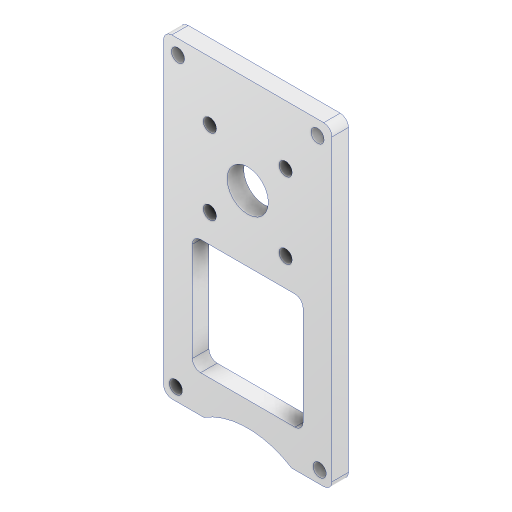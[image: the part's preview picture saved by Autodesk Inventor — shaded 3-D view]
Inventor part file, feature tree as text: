
AUTODESK INVENTOR PART (.ipt)
format: ipt  version: 2023.2 (Build 272271000, 271)  size: 305,664 bytes
history: native  units: mm
features: sketch x6, extrude x6, projected_geometry x4, fillet x1
ambient origin geometry x8: Origin, YZ Plane, XZ Plane, XY Plane, X Axis, Y Axis, Z Axis, Center Point
bodies: Body1 (feature_tree)
feature tree (17):
  sketch  "스케치1"
  extrude  "돌출2"  Depth=68.5mm
  sketch  "스케치4"
  extrude  "돌출4"  Depth=4.0mm TaperAngle=0.0deg
  extrude  "돌출3"  Depth=3.2mm
  extrude  "돌출6"  Depth=3.2mm
  fillet  "모깎기3"  Radius=3.2mm
  extrude  "돌출7"  Depth=3.2mm
  extrude  "돌출8"  Depth=3.0mm
  sketch  "스케치5"
  projected_geometry  "투영된 루프1"
  sketch  "스케치6"
  sketch  "스케치7"
  projected_geometry  "투영된 루프2"
  projected_geometry  "투영된 루프5"
  sketch  "스케치11"
  projected_geometry  "투영된 루프6"
